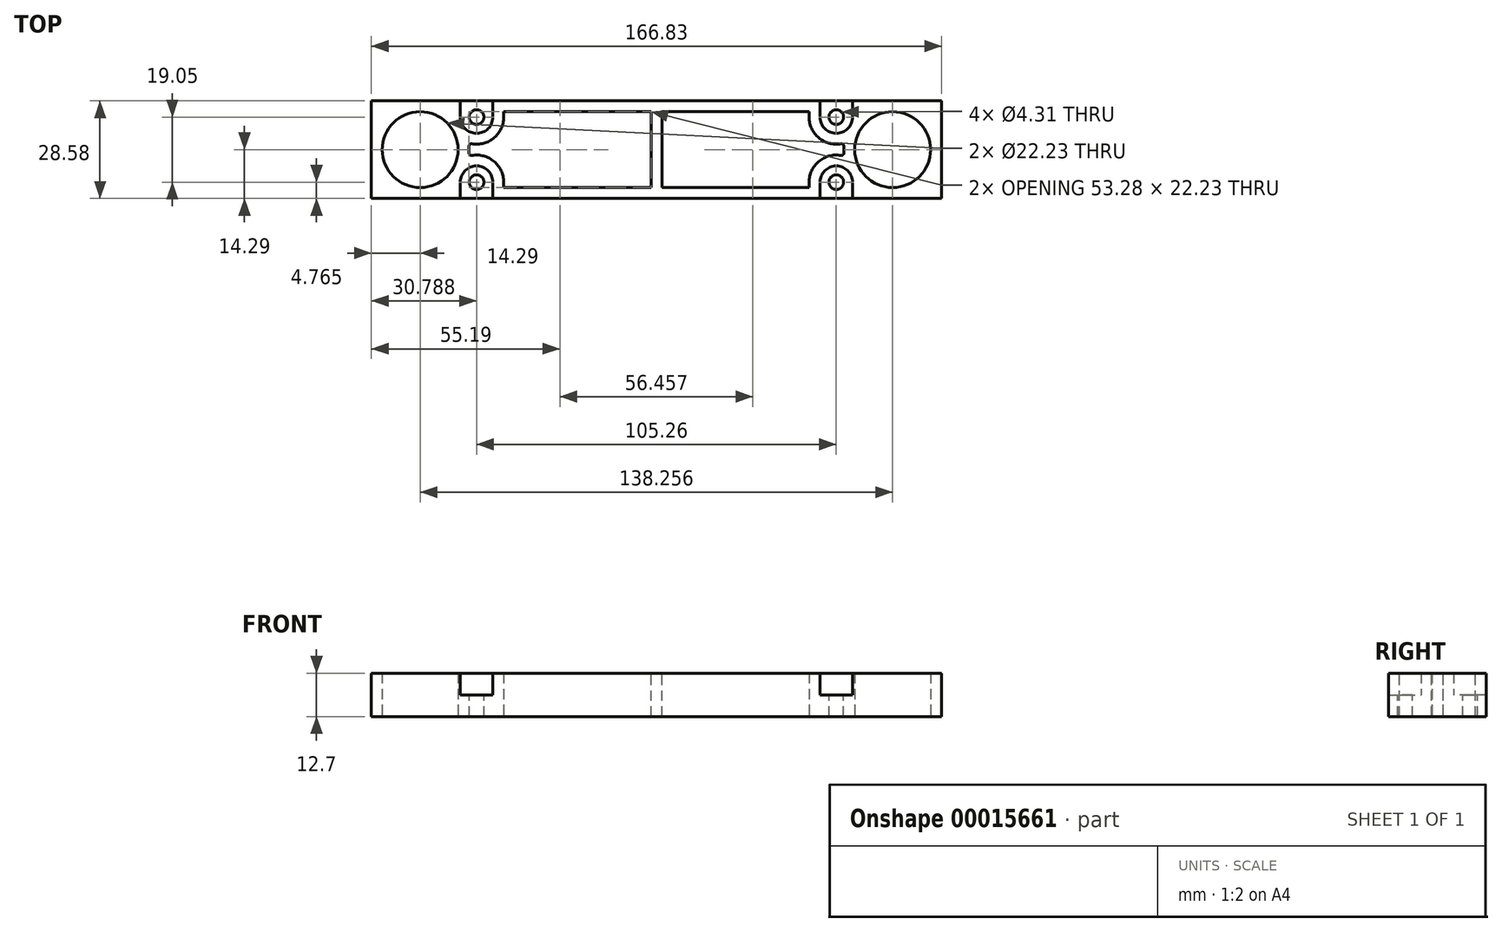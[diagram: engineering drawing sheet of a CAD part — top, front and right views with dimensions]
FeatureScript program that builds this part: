
annotation { "Feature Type Name" : "Feature", "Feature Type Description" : "" }
export const myFeature = defineFeature(function(context is Context, id is Id, definition is map)
    precondition{}
    {
        {
            var Q0;
            Q0=qCreatedBy(makeId("Top.planeOp"),FACE);
            var sketch = newSketch(context, id + "F0", { "sketchPlane" : qUnion([Q0])});
            skCircle(sketch, "E0", {"center": v(0, 0) * mm, "radius": 11.11 * mm});
            skLineSegment(sketch, "E1", {"start": v(0, 0) * mm, "end": v(138.26, 0) * mm, "construction": true});
            skLineSegment(sketch, "E2.left", {"start": v(-14.29, 14.29) * mm, "end": v(-14.29, -14.29) * mm});
            skLineSegment(sketch, "E2.right", {"start": v(152.54, 14.29) * mm, "end": v(152.54, -14.29) * mm});
            skPoint(sketch, "E2.middle", {"position": v(69.13, 0) * mm});
            skLineSegment(sketch, "E3", {"start": v(138.26, 0) * mm, "end": v(152.54, 0) * mm, "construction": true});
            skLineSegment(sketch, "E4", {"start": v(0, 0) * mm, "end": v(-14.29, 0) * mm, "construction": true});
            skCircle(sketch, "E5", {"center": v(138.26, 0) * mm, "radius": 11.11 * mm});
            skLineSegment(sketch, "E6", {"start": v(-14.29, 14.29) * mm, "end": v(11.74, 14.29) * mm});
            skLineSegment(sketch, "E7", {"start": v(152.54, 14.29) * mm, "end": v(126.52, 14.29) * mm});
            skLineSegment(sketch, "E8.bottom", {"start": v(11.74, 14.29) * mm, "end": v(21.26, 14.29) * mm, "construction": true});
            skLineSegment(sketch, "E8.top", {"start": v(11.74, 9.53) * mm, "end": v(21.26, 9.53) * mm, "construction": true});
            skLineSegment(sketch, "E8.left", {"start": v(11.74, 14.29) * mm, "end": v(11.74, 9.52) * mm});
            skLineSegment(sketch, "E8.right", {"start": v(21.26, 14.29) * mm, "end": v(21.26, 9.52) * mm});
            skLineSegment(sketch, "E9.bottom", {"start": v(126.52, 14.29) * mm, "end": v(117, 14.29) * mm, "construction": true});
            skLineSegment(sketch, "E9.top", {"start": v(126.52, 9.52) * mm, "end": v(117, 9.52) * mm, "construction": true});
            skLineSegment(sketch, "E9.left", {"start": v(126.52, 14.29) * mm, "end": v(126.52, 9.53) * mm});
            skLineSegment(sketch, "E9.right", {"start": v(117, 14.29) * mm, "end": v(117, 9.53) * mm});
            skCircle(sketch, "E10", {"center": v(16.5, 9.53) * mm, "radius": 7.94 * mm, "construction": true});
            skArc(sketch, "E11", {"start": v(21.26, 9.52) * mm, "mid": v(16.5, 14.29) * mm, "end": v(11.74, 9.53) * mm, "construction": true});
            skArc(sketch, "E12", {"start": v(11.74, 9.52) * mm, "mid": v(16.5, 4.76) * mm, "end": v(21.26, 9.52) * mm});
            skArc(sketch, "E13", {"start": v(117, 9.53) * mm, "mid": v(121.76, 4.76) * mm, "end": v(126.52, 9.53) * mm});
            skLineSegment(sketch, "E14", {"start": v(21.26, 14.29) * mm, "end": v(117, 14.29) * mm});
            skLineSegment(sketch, "E15", {"start": v(-14.29, -14.29) * mm, "end": v(11.74, -14.29) * mm});
            skLineSegment(sketch, "E16", {"start": v(152.54, -14.29) * mm, "end": v(126.52, -14.29) * mm});
            skLineSegment(sketch, "E17.bottom", {"start": v(11.74, -14.29) * mm, "end": v(21.26, -14.29) * mm, "construction": true});
            skLineSegment(sketch, "E17.top", {"start": v(11.74, -9.52) * mm, "end": v(21.26, -9.52) * mm, "construction": true});
            skLineSegment(sketch, "E17.left", {"start": v(11.74, -14.29) * mm, "end": v(11.74, -9.52) * mm});
            skLineSegment(sketch, "E17.right", {"start": v(21.26, -14.29) * mm, "end": v(21.26, -9.53) * mm});
            skLineSegment(sketch, "E18.bottom", {"start": v(126.52, -14.29) * mm, "end": v(117, -14.29) * mm, "construction": true});
            skLineSegment(sketch, "E18.top", {"start": v(126.52, -9.52) * mm, "end": v(117, -9.52) * mm, "construction": true});
            skLineSegment(sketch, "E18.left", {"start": v(126.52, -14.29) * mm, "end": v(126.52, -9.53) * mm});
            skLineSegment(sketch, "E18.right", {"start": v(117, -14.29) * mm, "end": v(117, -9.53) * mm});
            skLineSegment(sketch, "E19", {"start": v(21.26, -14.29) * mm, "end": v(117, -14.29) * mm});
            skArc(sketch, "E20", {"start": v(21.26, -9.53) * mm, "mid": v(16.5, -4.76) * mm, "end": v(11.74, -9.52) * mm});
            skArc(sketch, "E21", {"start": v(126.52, -9.53) * mm, "mid": v(121.76, -4.76) * mm, "end": v(117, -9.53) * mm});
            skSolve(sketch);
        }
        {
            var Q0;
            Q0 = qSketchRegion(id + "F0", true);
            extrude(context, id + "F1", {"entities" : qUnion([Q0]), "depth" : 6.35 * mm});
        }
        {
            var Q0;
            Q0=makeQuery(id+"F1.opExtrude","CAP_FACE",FACE,{"disambiguationData":[OSD([sQuery(id+"F0.wireOp",EDGE,"E0"),sQuery(id+"F0.wireOp",EDGE,"E2.left"),sQuery(id+"F0.wireOp",EDGE,"E2.right"),sQuery(id+"F0.wireOp",EDGE,"E5"),sQuery(id+"F0.wireOp",EDGE,"E6"),sQuery(id+"F0.wireOp",EDGE,"E7"),sQuery(id+"F0.wireOp",EDGE,"E8.left"),sQuery(id+"F0.wireOp",EDGE,"E8.right"),sQuery(id+"F0.wireOp",EDGE,"E9.left"),sQuery(id+"F0.wireOp",EDGE,"E9.right"),sQuery(id+"F0.wireOp",EDGE,"E12"),sQuery(id+"F0.wireOp",EDGE,"E13"),sQuery(id+"F0.wireOp",EDGE,"E14"),sQuery(id+"F0.wireOp",EDGE,"E15"),sQuery(id+"F0.wireOp",EDGE,"E16"),sQuery(id+"F0.wireOp",EDGE,"E17.left"),sQuery(id+"F0.wireOp",EDGE,"E17.right"),sQuery(id+"F0.wireOp",EDGE,"E18.left"),sQuery(id+"F0.wireOp",EDGE,"E18.right"),sQuery(id+"F0.wireOp",EDGE,"E19"),sQuery(id+"F0.wireOp",EDGE,"E20"),sQuery(id+"F0.wireOp",EDGE,"E21")])],"isStart":false});
            shell(context, id + "F2", {"entities" : qUnion([Q0]), "thickness" : 3.17 * mm});
        }
        {
            var Q0;
            Q0=makeQuery(id+"F2.opShell","OFFSET_FACE",FACE,{"disambiguationData":[OSD([sQuery(id+"F0.wireOp",EDGE,"E0"),sQuery(id+"F0.wireOp",EDGE,"E2.left"),sQuery(id+"F0.wireOp",EDGE,"E2.right"),sQuery(id+"F0.wireOp",EDGE,"E5"),sQuery(id+"F0.wireOp",EDGE,"E6"),sQuery(id+"F0.wireOp",EDGE,"E7"),sQuery(id+"F0.wireOp",EDGE,"E8.left"),sQuery(id+"F0.wireOp",EDGE,"E8.right"),sQuery(id+"F0.wireOp",EDGE,"E9.left"),sQuery(id+"F0.wireOp",EDGE,"E9.right"),sQuery(id+"F0.wireOp",EDGE,"E12"),sQuery(id+"F0.wireOp",EDGE,"E13"),sQuery(id+"F0.wireOp",EDGE,"E14"),sQuery(id+"F0.wireOp",EDGE,"E15"),sQuery(id+"F0.wireOp",EDGE,"E16"),sQuery(id+"F0.wireOp",EDGE,"E17.left"),sQuery(id+"F0.wireOp",EDGE,"E17.right"),sQuery(id+"F0.wireOp",EDGE,"E18.left"),sQuery(id+"F0.wireOp",EDGE,"E18.right"),sQuery(id+"F0.wireOp",EDGE,"E19"),sQuery(id+"F0.wireOp",EDGE,"E20"),sQuery(id+"F0.wireOp",EDGE,"E21")]),OD(0.0)]});
            var Q1;
            Q1=makeQuery(id+"F2.opShell","OFFSET_FACE",FACE,{"disambiguationData":[OSD([sQuery(id+"F0.wireOp",EDGE,"E0"),sQuery(id+"F0.wireOp",EDGE,"E2.left"),sQuery(id+"F0.wireOp",EDGE,"E2.right"),sQuery(id+"F0.wireOp",EDGE,"E5"),sQuery(id+"F0.wireOp",EDGE,"E6"),sQuery(id+"F0.wireOp",EDGE,"E7"),sQuery(id+"F0.wireOp",EDGE,"E8.left"),sQuery(id+"F0.wireOp",EDGE,"E8.right"),sQuery(id+"F0.wireOp",EDGE,"E9.left"),sQuery(id+"F0.wireOp",EDGE,"E9.right"),sQuery(id+"F0.wireOp",EDGE,"E12"),sQuery(id+"F0.wireOp",EDGE,"E13"),sQuery(id+"F0.wireOp",EDGE,"E14"),sQuery(id+"F0.wireOp",EDGE,"E15"),sQuery(id+"F0.wireOp",EDGE,"E16"),sQuery(id+"F0.wireOp",EDGE,"E17.left"),sQuery(id+"F0.wireOp",EDGE,"E17.right"),sQuery(id+"F0.wireOp",EDGE,"E18.left"),sQuery(id+"F0.wireOp",EDGE,"E18.right"),sQuery(id+"F0.wireOp",EDGE,"E19"),sQuery(id+"F0.wireOp",EDGE,"E20"),sQuery(id+"F0.wireOp",EDGE,"E21")]),OD(3.0)]});
            var Q2;
            Q2=makeQuery(id+"F2.opShell","OFFSET_FACE",FACE,{"disambiguationData":[OSD([sQuery(id+"F0.wireOp",EDGE,"E0"),sQuery(id+"F0.wireOp",EDGE,"E2.left"),sQuery(id+"F0.wireOp",EDGE,"E2.right"),sQuery(id+"F0.wireOp",EDGE,"E5"),sQuery(id+"F0.wireOp",EDGE,"E6"),sQuery(id+"F0.wireOp",EDGE,"E7"),sQuery(id+"F0.wireOp",EDGE,"E8.left"),sQuery(id+"F0.wireOp",EDGE,"E8.right"),sQuery(id+"F0.wireOp",EDGE,"E9.left"),sQuery(id+"F0.wireOp",EDGE,"E9.right"),sQuery(id+"F0.wireOp",EDGE,"E12"),sQuery(id+"F0.wireOp",EDGE,"E13"),sQuery(id+"F0.wireOp",EDGE,"E14"),sQuery(id+"F0.wireOp",EDGE,"E15"),sQuery(id+"F0.wireOp",EDGE,"E16"),sQuery(id+"F0.wireOp",EDGE,"E17.left"),sQuery(id+"F0.wireOp",EDGE,"E17.right"),sQuery(id+"F0.wireOp",EDGE,"E18.left"),sQuery(id+"F0.wireOp",EDGE,"E18.right"),sQuery(id+"F0.wireOp",EDGE,"E19"),sQuery(id+"F0.wireOp",EDGE,"E20"),sQuery(id+"F0.wireOp",EDGE,"E21")]),OD(4.0)]});
            var Q3;
            Q3=makeQuery(id+"F2.opShell","OFFSET_FACE",FACE,{"disambiguationData":[OSD([sQuery(id+"F0.wireOp",EDGE,"E0"),sQuery(id+"F0.wireOp",EDGE,"E2.left"),sQuery(id+"F0.wireOp",EDGE,"E2.right"),sQuery(id+"F0.wireOp",EDGE,"E5"),sQuery(id+"F0.wireOp",EDGE,"E6"),sQuery(id+"F0.wireOp",EDGE,"E7"),sQuery(id+"F0.wireOp",EDGE,"E8.left"),sQuery(id+"F0.wireOp",EDGE,"E8.right"),sQuery(id+"F0.wireOp",EDGE,"E9.left"),sQuery(id+"F0.wireOp",EDGE,"E9.right"),sQuery(id+"F0.wireOp",EDGE,"E12"),sQuery(id+"F0.wireOp",EDGE,"E13"),sQuery(id+"F0.wireOp",EDGE,"E14"),sQuery(id+"F0.wireOp",EDGE,"E15"),sQuery(id+"F0.wireOp",EDGE,"E16"),sQuery(id+"F0.wireOp",EDGE,"E17.left"),sQuery(id+"F0.wireOp",EDGE,"E17.right"),sQuery(id+"F0.wireOp",EDGE,"E18.left"),sQuery(id+"F0.wireOp",EDGE,"E18.right"),sQuery(id+"F0.wireOp",EDGE,"E19"),sQuery(id+"F0.wireOp",EDGE,"E20"),sQuery(id+"F0.wireOp",EDGE,"E21")]),OD(1.0)]});
            var Q4;
            Q4=makeQuery(id+"F1.opExtrude","CAP_FACE",FACE,{"disambiguationData":[OSD([sQuery(id+"F0.wireOp",EDGE,"E0"),sQuery(id+"F0.wireOp",EDGE,"E2.left"),sQuery(id+"F0.wireOp",EDGE,"E2.right"),sQuery(id+"F0.wireOp",EDGE,"E5"),sQuery(id+"F0.wireOp",EDGE,"E6"),sQuery(id+"F0.wireOp",EDGE,"E7"),sQuery(id+"F0.wireOp",EDGE,"E8.left"),sQuery(id+"F0.wireOp",EDGE,"E8.right"),sQuery(id+"F0.wireOp",EDGE,"E9.left"),sQuery(id+"F0.wireOp",EDGE,"E9.right"),sQuery(id+"F0.wireOp",EDGE,"E12"),sQuery(id+"F0.wireOp",EDGE,"E13"),sQuery(id+"F0.wireOp",EDGE,"E14"),sQuery(id+"F0.wireOp",EDGE,"E15"),sQuery(id+"F0.wireOp",EDGE,"E16"),sQuery(id+"F0.wireOp",EDGE,"E17.left"),sQuery(id+"F0.wireOp",EDGE,"E17.right"),sQuery(id+"F0.wireOp",EDGE,"E18.left"),sQuery(id+"F0.wireOp",EDGE,"E18.right"),sQuery(id+"F0.wireOp",EDGE,"E19"),sQuery(id+"F0.wireOp",EDGE,"E20"),sQuery(id+"F0.wireOp",EDGE,"E21")])],"isStart":false});
            extrude(context, id + "F3", {"entities" : qUnion([Q0, Q1, Q2, Q3]), "operationType" : NewBodyOperationType.ADD, "endBound" : BoundingType.UP_TO_SURFACE, "endBoundEntityFace" : qUnion([Q4]), "depth" : 25.4 * mm});
        }
        {
            var Q0;
            Q0=makeQuery(id+"F2.opShell","OFFSET_FACE",FACE,{"disambiguationData":[OSD([sQuery(id+"F0.wireOp",EDGE,"E0"),sQuery(id+"F0.wireOp",EDGE,"E2.left"),sQuery(id+"F0.wireOp",EDGE,"E2.right"),sQuery(id+"F0.wireOp",EDGE,"E5"),sQuery(id+"F0.wireOp",EDGE,"E6"),sQuery(id+"F0.wireOp",EDGE,"E7"),sQuery(id+"F0.wireOp",EDGE,"E8.left"),sQuery(id+"F0.wireOp",EDGE,"E8.right"),sQuery(id+"F0.wireOp",EDGE,"E9.left"),sQuery(id+"F0.wireOp",EDGE,"E9.right"),sQuery(id+"F0.wireOp",EDGE,"E12"),sQuery(id+"F0.wireOp",EDGE,"E13"),sQuery(id+"F0.wireOp",EDGE,"E14"),sQuery(id+"F0.wireOp",EDGE,"E15"),sQuery(id+"F0.wireOp",EDGE,"E16"),sQuery(id+"F0.wireOp",EDGE,"E17.left"),sQuery(id+"F0.wireOp",EDGE,"E17.right"),sQuery(id+"F0.wireOp",EDGE,"E18.left"),sQuery(id+"F0.wireOp",EDGE,"E18.right"),sQuery(id+"F0.wireOp",EDGE,"E19"),sQuery(id+"F0.wireOp",EDGE,"E20"),sQuery(id+"F0.wireOp",EDGE,"E21")]),OD(2.0)]});
            var Q1;
            Q1=makeQuery(id+"F1.opExtrude","CAP_FACE",FACE,{"disambiguationData":[OSD([sQuery(id+"F0.wireOp",EDGE,"E0"),sQuery(id+"F0.wireOp",EDGE,"E2.left"),sQuery(id+"F0.wireOp",EDGE,"E2.right"),sQuery(id+"F0.wireOp",EDGE,"E5"),sQuery(id+"F0.wireOp",EDGE,"E6"),sQuery(id+"F0.wireOp",EDGE,"E7"),sQuery(id+"F0.wireOp",EDGE,"E8.left"),sQuery(id+"F0.wireOp",EDGE,"E8.right"),sQuery(id+"F0.wireOp",EDGE,"E9.left"),sQuery(id+"F0.wireOp",EDGE,"E9.right"),sQuery(id+"F0.wireOp",EDGE,"E12"),sQuery(id+"F0.wireOp",EDGE,"E13"),sQuery(id+"F0.wireOp",EDGE,"E14"),sQuery(id+"F0.wireOp",EDGE,"E15"),sQuery(id+"F0.wireOp",EDGE,"E16"),sQuery(id+"F0.wireOp",EDGE,"E17.left"),sQuery(id+"F0.wireOp",EDGE,"E17.right"),sQuery(id+"F0.wireOp",EDGE,"E18.left"),sQuery(id+"F0.wireOp",EDGE,"E18.right"),sQuery(id+"F0.wireOp",EDGE,"E19"),sQuery(id+"F0.wireOp",EDGE,"E20"),sQuery(id+"F0.wireOp",EDGE,"E21")])],"isStart":true});
            extrude(context, id + "F4", {"entities" : qUnion([Q0]), "operationType" : NewBodyOperationType.REMOVE, "endBound" : BoundingType.UP_TO_SURFACE, "oppositeDirection" : true, "endBoundEntityFace" : qUnion([Q1]), "depth" : 25.4 * mm});
        }
        {
            var Q0;
            Q0=makeQuery(id+"F1.opExtrude","CAP_FACE",FACE,{"disambiguationData":[OSD([sQuery(id+"F0.wireOp",EDGE,"E0"),sQuery(id+"F0.wireOp",EDGE,"E2.left"),sQuery(id+"F0.wireOp",EDGE,"E2.right"),sQuery(id+"F0.wireOp",EDGE,"E5"),sQuery(id+"F0.wireOp",EDGE,"E6"),sQuery(id+"F0.wireOp",EDGE,"E7"),sQuery(id+"F0.wireOp",EDGE,"E8.left"),sQuery(id+"F0.wireOp",EDGE,"E8.right"),sQuery(id+"F0.wireOp",EDGE,"E9.left"),sQuery(id+"F0.wireOp",EDGE,"E9.right"),sQuery(id+"F0.wireOp",EDGE,"E12"),sQuery(id+"F0.wireOp",EDGE,"E13"),sQuery(id+"F0.wireOp",EDGE,"E14"),sQuery(id+"F0.wireOp",EDGE,"E15"),sQuery(id+"F0.wireOp",EDGE,"E16"),sQuery(id+"F0.wireOp",EDGE,"E17.left"),sQuery(id+"F0.wireOp",EDGE,"E17.right"),sQuery(id+"F0.wireOp",EDGE,"E18.left"),sQuery(id+"F0.wireOp",EDGE,"E18.right"),sQuery(id+"F0.wireOp",EDGE,"E19"),sQuery(id+"F0.wireOp",EDGE,"E20"),sQuery(id+"F0.wireOp",EDGE,"E21")])],"isStart":true});
            var sketch = newSketch(context, id + "F5", { "sketchPlane" : qUnion([Q0])});
            skLineSegment(sketch, "E22.bottom", {"start": v(11.74, -14.29) * mm, "end": v(126.52, -14.29) * mm});
            skLineSegment(sketch, "E22.top", {"start": v(11.74, 14.29) * mm, "end": v(126.52, 14.29) * mm});
            skLineSegment(sketch, "E22.left", {"start": v(11.74, -14.29) * mm, "end": v(11.74, 14.29) * mm, "construction": true});
            skLineSegment(sketch, "E22.right", {"start": v(126.52, -14.29) * mm, "end": v(126.52, 14.29) * mm, "construction": true});
            skCircle(sketch, "E23", {"center": v(16.5, 9.52) * mm, "radius": 2.15 * mm});
            skCircle(sketch, "E24", {"center": v(16.5, -9.53) * mm, "radius": 2.15 * mm});
            skCircle(sketch, "E25", {"center": v(121.76, 9.53) * mm, "radius": 2.15 * mm});
            skCircle(sketch, "E26", {"center": v(121.76, -9.53) * mm, "radius": 2.15 * mm});
            skSolve(sketch);
        }
        {
            var Q0;
            {var subQ19=sQuery(id+"F0.wireOp",EDGE,"E0");var subQ20=makeQuery(id+"F1.opExtrude","CAP_EDGE",EDGE,{"disambiguationData":[OSD([subQ19])],"isStart":true});Q0=makeQuery(id+"F5.imprint","IMPRINT",FACE,{"disambiguationData":[TD([[makeQuery(id+"F5.imprint","IMPRINT",EDGE,{"derivedFrom":subQ20}),1.0]])]});}
            var Q1;
            Q1=makeQuery(id+"F5.imprint","IMPRINT",FACE,{"disambiguationData":[TD([[makeQuery(id+"F5.imprint","IMPRINT",EDGE,{"derivedFrom":sQuery(id+"F5.wireOp",EDGE,"E24")}),-1.0]])]});
            var Q2;
            Q2=makeQuery(id+"F5.imprint","IMPRINT",FACE,{"disambiguationData":[TD([[makeQuery(id+"F5.imprint","IMPRINT",EDGE,{"derivedFrom":sQuery(id+"F5.wireOp",EDGE,"E26")}),-1.0]])]});
            var Q3;
            Q3=makeQuery(id+"F5.imprint","IMPRINT",FACE,{"disambiguationData":[TD([[makeQuery(id+"F5.imprint","IMPRINT",EDGE,{"derivedFrom":sQuery(id+"F5.wireOp",EDGE,"E25")}),-1.0]])]});
            var Q4;
            Q4=makeQuery(id+"F5.imprint","IMPRINT",FACE,{"disambiguationData":[TD([[makeQuery(id+"F5.imprint","IMPRINT",EDGE,{"derivedFrom":sQuery(id+"F5.wireOp",EDGE,"E23")}),-1.0]])]});
            extrude(context, id + "F6", {"entities" : qUnion([Q0, Q1, Q2, Q3, Q4]), "operationType" : NewBodyOperationType.ADD, "depth" : 6.35 * mm});
        }
        {
            var Q0;
            {var subQ0=sQuery(id+"F0.wireOp",EDGE,"E21");var subQ1=sQuery(id+"F0.wireOp",EDGE,"E20");var subQ2=sQuery(id+"F0.wireOp",EDGE,"E19");var subQ3=sQuery(id+"F0.wireOp",EDGE,"E18.right");var subQ4=sQuery(id+"F0.wireOp",EDGE,"E18.left");var subQ5=sQuery(id+"F0.wireOp",EDGE,"E17.right");var subQ6=sQuery(id+"F0.wireOp",EDGE,"E17.left");var subQ7=sQuery(id+"F0.wireOp",EDGE,"E16");var subQ8=sQuery(id+"F0.wireOp",EDGE,"E15");var subQ9=sQuery(id+"F0.wireOp",EDGE,"E14");var subQ10=sQuery(id+"F0.wireOp",EDGE,"E13");var subQ11=sQuery(id+"F0.wireOp",EDGE,"E12");var subQ12=sQuery(id+"F0.wireOp",EDGE,"E9.right");var subQ13=sQuery(id+"F0.wireOp",EDGE,"E9.left");var subQ14=sQuery(id+"F0.wireOp",EDGE,"E8.right");var subQ15=sQuery(id+"F0.wireOp",EDGE,"E8.left");var subQ16=sQuery(id+"F0.wireOp",EDGE,"E7");var subQ17=sQuery(id+"F0.wireOp",EDGE,"E6");var subQ18=sQuery(id+"F0.wireOp",EDGE,"E5");var subQ19=sQuery(id+"F0.wireOp",EDGE,"E2.right");var subQ20=sQuery(id+"F0.wireOp",EDGE,"E2.left");var subQ21=sQuery(id+"F0.wireOp",EDGE,"E0");Q0=makeQuery(id+"F3.boolean.opBoolean","MERGE",FACE,{"derivedFrom":[makeQuery(id+"F1.opExtrude","CAP_FACE",FACE,{"disambiguationData":[OSD([subQ21,subQ20,subQ19,subQ18,subQ17,subQ16,subQ15,subQ14,subQ13,subQ12,subQ11,subQ10,subQ9,subQ8,subQ7,subQ6,subQ5,subQ4,subQ3,subQ2,subQ1,subQ0])],"isStart":false}),makeQuery(id+"F3.opExtrude","CAP_FACE",FACE,{"disambiguationData":[OSD([subQ21,subQ20,subQ19,subQ18,subQ17,subQ16,subQ15,subQ14,subQ13,subQ12,subQ11,subQ10,subQ9,subQ8,subQ7,subQ6,subQ5,subQ4,subQ3,subQ2,subQ1,subQ0]),ownerDisambiguation([makeQuery(id+"F3.opExtrude","SWEPT_BODY",BODY,{"disambiguationData":[OSD([subQ21,subQ20,subQ19,subQ18,subQ17,subQ16,subQ15,subQ14,subQ13,subQ12,subQ11,subQ10,subQ9,subQ8,subQ7,subQ6,subQ5,subQ4,subQ3,subQ2,subQ1,subQ0]),TDD([makeQuery(id+"F2.opShell","OFFSET_FACE",FACE,{"disambiguationData":[OSD([subQ21,subQ20,subQ19,subQ18,subQ17,subQ16,subQ15,subQ14,subQ13,subQ12,subQ11,subQ10,subQ9,subQ8,subQ7,subQ6,subQ5,subQ4,subQ3,subQ2,subQ1,subQ0]),OD(0.0)]})])]})])],"isStart":false}),makeQuery(id+"F3.opExtrude","CAP_FACE",FACE,{"disambiguationData":[OSD([subQ21,subQ20,subQ19,subQ18,subQ17,subQ16,subQ15,subQ14,subQ13,subQ12,subQ11,subQ10,subQ9,subQ8,subQ7,subQ6,subQ5,subQ4,subQ3,subQ2,subQ1,subQ0]),ownerDisambiguation([makeQuery(id+"F3.opExtrude","SWEPT_BODY",BODY,{"disambiguationData":[OSD([subQ21,subQ20,subQ19,subQ18,subQ17,subQ16,subQ15,subQ14,subQ13,subQ12,subQ11,subQ10,subQ9,subQ8,subQ7,subQ6,subQ5,subQ4,subQ3,subQ2,subQ1,subQ0]),TDD([makeQuery(id+"F2.opShell","OFFSET_FACE",FACE,{"disambiguationData":[OSD([subQ21,subQ20,subQ19,subQ18,subQ17,subQ16,subQ15,subQ14,subQ13,subQ12,subQ11,subQ10,subQ9,subQ8,subQ7,subQ6,subQ5,subQ4,subQ3,subQ2,subQ1,subQ0]),OD(1.0)]})])]})])],"isStart":false}),makeQuery(id+"F3.opExtrude","CAP_FACE",FACE,{"disambiguationData":[OSD([subQ21,subQ20,subQ19,subQ18,subQ17,subQ16,subQ15,subQ14,subQ13,subQ12,subQ11,subQ10,subQ9,subQ8,subQ7,subQ6,subQ5,subQ4,subQ3,subQ2,subQ1,subQ0]),ownerDisambiguation([makeQuery(id+"F3.opExtrude","SWEPT_BODY",BODY,{"disambiguationData":[OSD([subQ21,subQ20,subQ19,subQ18,subQ17,subQ16,subQ15,subQ14,subQ13,subQ12,subQ11,subQ10,subQ9,subQ8,subQ7,subQ6,subQ5,subQ4,subQ3,subQ2,subQ1,subQ0]),TDD([makeQuery(id+"F2.opShell","OFFSET_FACE",FACE,{"disambiguationData":[OSD([subQ21,subQ20,subQ19,subQ18,subQ17,subQ16,subQ15,subQ14,subQ13,subQ12,subQ11,subQ10,subQ9,subQ8,subQ7,subQ6,subQ5,subQ4,subQ3,subQ2,subQ1,subQ0]),OD(3.0)]})])]})])],"isStart":false}),makeQuery(id+"F3.opExtrude","CAP_FACE",FACE,{"disambiguationData":[OSD([subQ21,subQ20,subQ19,subQ18,subQ17,subQ16,subQ15,subQ14,subQ13,subQ12,subQ11,subQ10,subQ9,subQ8,subQ7,subQ6,subQ5,subQ4,subQ3,subQ2,subQ1,subQ0]),ownerDisambiguation([makeQuery(id+"F3.opExtrude","SWEPT_BODY",BODY,{"disambiguationData":[OSD([subQ21,subQ20,subQ19,subQ18,subQ17,subQ16,subQ15,subQ14,subQ13,subQ12,subQ11,subQ10,subQ9,subQ8,subQ7,subQ6,subQ5,subQ4,subQ3,subQ2,subQ1,subQ0]),TDD([makeQuery(id+"F2.opShell","OFFSET_FACE",FACE,{"disambiguationData":[OSD([subQ21,subQ20,subQ19,subQ18,subQ17,subQ16,subQ15,subQ14,subQ13,subQ12,subQ11,subQ10,subQ9,subQ8,subQ7,subQ6,subQ5,subQ4,subQ3,subQ2,subQ1,subQ0]),OD(4.0)]})])]})])],"isStart":false})]});}
            var sketch = newSketch(context, id + "F7", { "sketchPlane" : qUnion([Q0])});
            skLineSegment(sketch, "E27.bottom", {"start": v(67.54, 11.11) * mm, "end": v(70.72, 11.11) * mm});
            skLineSegment(sketch, "E27.top", {"start": v(67.54, -11.11) * mm, "end": v(70.72, -11.11) * mm});
            skLineSegment(sketch, "E27.left", {"start": v(67.54, 11.11) * mm, "end": v(67.54, -11.11) * mm});
            skLineSegment(sketch, "E27.right", {"start": v(70.72, 11.11) * mm, "end": v(70.72, -11.11) * mm});
            skPoint(sketch, "E28", {"position": v(69.13, 11.11) * mm});
            skSolve(sketch);
        }
        {
            var Q0;
            Q0 = qSketchRegion(id + "F7", true);
            var Q1;
            Q1=makeQuery(id+"F6.opExtrude","CAP_FACE",FACE,{"disambiguationData":[OSD([sQuery(id+"F0.wireOp",EDGE,"E0"),sQuery(id+"F0.wireOp",EDGE,"E2.left"),sQuery(id+"F0.wireOp",EDGE,"E2.right"),sQuery(id+"F0.wireOp",EDGE,"E5"),sQuery(id+"F0.wireOp",EDGE,"E6"),sQuery(id+"F0.wireOp",EDGE,"E7"),sQuery(id+"F0.wireOp",EDGE,"E8.left"),sQuery(id+"F0.wireOp",EDGE,"E8.right"),sQuery(id+"F0.wireOp",EDGE,"E9.left"),sQuery(id+"F0.wireOp",EDGE,"E9.right"),sQuery(id+"F0.wireOp",EDGE,"E12"),sQuery(id+"F0.wireOp",EDGE,"E13"),sQuery(id+"F0.wireOp",EDGE,"E14"),sQuery(id+"F0.wireOp",EDGE,"E15"),sQuery(id+"F0.wireOp",EDGE,"E16"),sQuery(id+"F0.wireOp",EDGE,"E17.left"),sQuery(id+"F0.wireOp",EDGE,"E17.right"),sQuery(id+"F0.wireOp",EDGE,"E18.left"),sQuery(id+"F0.wireOp",EDGE,"E18.right"),sQuery(id+"F0.wireOp",EDGE,"E19"),sQuery(id+"F0.wireOp",EDGE,"E20"),sQuery(id+"F0.wireOp",EDGE,"E21"),sQuery(id+"F5.wireOp",EDGE,"E22.bottom"),sQuery(id+"F5.wireOp",EDGE,"E22.top"),sQuery(id+"F5.wireOp",EDGE,"E23"),sQuery(id+"F5.wireOp",EDGE,"E24"),sQuery(id+"F5.wireOp",EDGE,"E25"),sQuery(id+"F5.wireOp",EDGE,"E26")])],"isStart":false});
            extrude(context, id + "F8", {"entities" : qUnion([Q0]), "operationType" : NewBodyOperationType.ADD, "endBound" : BoundingType.UP_TO_SURFACE, "oppositeDirection" : true, "endBoundEntityFace" : qUnion([Q1]), "depth" : 25.4 * mm});
        }
        {
            var Q0;
            {var subQ0=sQuery(id+"F0.wireOp",EDGE,"E0");var subQ1=sQuery(id+"F0.wireOp",EDGE,"E21");var subQ2=sQuery(id+"F0.wireOp",EDGE,"E20");var subQ3=sQuery(id+"F0.wireOp",EDGE,"E19");var subQ4=sQuery(id+"F0.wireOp",EDGE,"E18.right");var subQ5=sQuery(id+"F0.wireOp",EDGE,"E18.left");var subQ6=sQuery(id+"F0.wireOp",EDGE,"E17.right");var subQ7=sQuery(id+"F0.wireOp",EDGE,"E17.left");var subQ8=sQuery(id+"F0.wireOp",EDGE,"E16");var subQ9=sQuery(id+"F0.wireOp",EDGE,"E15");var subQ10=sQuery(id+"F0.wireOp",EDGE,"E14");var subQ11=sQuery(id+"F0.wireOp",EDGE,"E13");var subQ12=sQuery(id+"F0.wireOp",EDGE,"E12");var subQ13=sQuery(id+"F0.wireOp",EDGE,"E9.right");var subQ14=sQuery(id+"F0.wireOp",EDGE,"E9.left");var subQ15=sQuery(id+"F0.wireOp",EDGE,"E8.right");var subQ16=sQuery(id+"F0.wireOp",EDGE,"E8.left");var subQ17=sQuery(id+"F0.wireOp",EDGE,"E7");var subQ18=sQuery(id+"F0.wireOp",EDGE,"E6");var subQ19=sQuery(id+"F0.wireOp",EDGE,"E5");var subQ20=sQuery(id+"F0.wireOp",EDGE,"E2.right");var subQ21=sQuery(id+"F0.wireOp",EDGE,"E2.left");var subQ22=makeQuery(id+"F1.opExtrude","CAP_FACE",FACE,{"disambiguationData":[OSD([subQ0,subQ21,subQ20,subQ19,subQ18,subQ17,subQ16,subQ15,subQ14,subQ13,subQ12,subQ11,subQ10,subQ9,subQ8,subQ7,subQ6,subQ5,subQ4,subQ3,subQ2,subQ1])],"isStart":true});var subQ23=makeQuery(id+"F1.opExtrude","SWEPT_FACE",FACE,{"disambiguationData":[OSD([subQ12])]});var subQ24=makeQuery(id+"F1.opExtrude","SWEPT_FACE",FACE,{"disambiguationData":[OSD([subQ0])]});Q0=makeQuery(id+"F6.boolean.opBoolean","MERGE",EDGE,{"derivedFrom":[makeQuery(id+"F4.boolean.opBoolean","MERGE",EDGE,{"derivedFrom":[makeQuery(id+"F2.opShell","TWEAK_EDGE",EDGE,{"derivedFrom":[subQ24,subQ23]}),makeQuery(id+"F4.opExtrude","SWEPT_EDGE",EDGE,{"disambiguationData":[OSD([subQ0,subQ21,subQ20,subQ19,subQ18,subQ17,subQ16,subQ15,subQ14,subQ13,subQ12,subQ11,subQ10,subQ9,subQ8,subQ7,subQ6,subQ5,subQ4,subQ3,subQ2,subQ1]),TDD([makeQuery(id+"F2.opShell","TWEAK_VERTEX",VERTEX,{"derivedFrom":[subQ24,subQ22,subQ23]})])]})]}),makeQuery(id+"F6.opExtrude","SWEPT_EDGE",EDGE,{"disambiguationData":[OSD([subQ0,subQ21,subQ20,subQ19,subQ18,subQ17,subQ16,subQ15,subQ14,subQ13,subQ12,subQ11,subQ10,subQ9,subQ8,subQ7,subQ6,subQ5,subQ4,subQ3,subQ2,subQ1]),TDD([makeQuery(id+"F5.imprint","INTERSECT",VERTEX,{"derivedFrom":[makeQuery(id+"F4.boolean.opBoolean","COPY",EDGE,{"derivedFrom":makeQuery(id+"F4.opExtrude","TWEAK_EDGE",EDGE,{"derivedFrom":[subQ22,makeQuery(id+"F2.opShell","OFFSET_EDGE",EDGE,{"disambiguationData":[OSD([subQ12]),TDD([makeQuery(id+"F1.opExtrude","CAP_EDGE",EDGE,{"disambiguationData":[OSD([subQ12])],"isStart":true})])]})]})}),makeQuery(id+"F4.boolean.opBoolean","COPY",EDGE,{"derivedFrom":makeQuery(id+"F4.opExtrude","TWEAK_EDGE",EDGE,{"derivedFrom":[subQ22,makeQuery(id+"F2.opShell","OFFSET_EDGE",EDGE,{"disambiguationData":[OSD([subQ0]),TDD([makeQuery(id+"F1.opExtrude","CAP_EDGE",EDGE,{"disambiguationData":[OSD([subQ0])],"isStart":true})]),OD(0.0)]})]})})]})])]})]});}
            var Q1;
            {var subQ0=sQuery(id+"F0.wireOp",EDGE,"E0");var subQ1=sQuery(id+"F0.wireOp",EDGE,"E21");var subQ2=sQuery(id+"F0.wireOp",EDGE,"E20");var subQ3=sQuery(id+"F0.wireOp",EDGE,"E19");var subQ4=sQuery(id+"F0.wireOp",EDGE,"E18.right");var subQ5=sQuery(id+"F0.wireOp",EDGE,"E18.left");var subQ6=sQuery(id+"F0.wireOp",EDGE,"E17.right");var subQ7=sQuery(id+"F0.wireOp",EDGE,"E17.left");var subQ8=sQuery(id+"F0.wireOp",EDGE,"E16");var subQ9=sQuery(id+"F0.wireOp",EDGE,"E15");var subQ10=sQuery(id+"F0.wireOp",EDGE,"E14");var subQ11=sQuery(id+"F0.wireOp",EDGE,"E13");var subQ12=sQuery(id+"F0.wireOp",EDGE,"E12");var subQ13=sQuery(id+"F0.wireOp",EDGE,"E9.right");var subQ14=sQuery(id+"F0.wireOp",EDGE,"E9.left");var subQ15=sQuery(id+"F0.wireOp",EDGE,"E8.right");var subQ16=sQuery(id+"F0.wireOp",EDGE,"E8.left");var subQ17=sQuery(id+"F0.wireOp",EDGE,"E7");var subQ18=sQuery(id+"F0.wireOp",EDGE,"E6");var subQ19=sQuery(id+"F0.wireOp",EDGE,"E5");var subQ20=sQuery(id+"F0.wireOp",EDGE,"E2.right");var subQ21=sQuery(id+"F0.wireOp",EDGE,"E2.left");var subQ22=makeQuery(id+"F1.opExtrude","CAP_FACE",FACE,{"disambiguationData":[OSD([subQ0,subQ21,subQ20,subQ19,subQ18,subQ17,subQ16,subQ15,subQ14,subQ13,subQ12,subQ11,subQ10,subQ9,subQ8,subQ7,subQ6,subQ5,subQ4,subQ3,subQ2,subQ1])],"isStart":true});var subQ23=makeQuery(id+"F1.opExtrude","SWEPT_FACE",FACE,{"disambiguationData":[OSD([subQ2])]});var subQ24=makeQuery(id+"F1.opExtrude","SWEPT_FACE",FACE,{"disambiguationData":[OSD([subQ0])]});Q1=makeQuery(id+"F6.boolean.opBoolean","MERGE",EDGE,{"derivedFrom":[makeQuery(id+"F4.boolean.opBoolean","MERGE",EDGE,{"derivedFrom":[makeQuery(id+"F2.opShell","TWEAK_EDGE",EDGE,{"derivedFrom":[subQ24,subQ23]}),makeQuery(id+"F4.opExtrude","SWEPT_EDGE",EDGE,{"disambiguationData":[OSD([subQ0,subQ21,subQ20,subQ19,subQ18,subQ17,subQ16,subQ15,subQ14,subQ13,subQ12,subQ11,subQ10,subQ9,subQ8,subQ7,subQ6,subQ5,subQ4,subQ3,subQ2,subQ1]),TDD([makeQuery(id+"F2.opShell","TWEAK_VERTEX",VERTEX,{"derivedFrom":[subQ24,subQ22,subQ23]})])]})]}),makeQuery(id+"F6.opExtrude","SWEPT_EDGE",EDGE,{"disambiguationData":[OSD([subQ0,subQ21,subQ20,subQ19,subQ18,subQ17,subQ16,subQ15,subQ14,subQ13,subQ12,subQ11,subQ10,subQ9,subQ8,subQ7,subQ6,subQ5,subQ4,subQ3,subQ2,subQ1]),TDD([makeQuery(id+"F5.imprint","INTERSECT",VERTEX,{"derivedFrom":[makeQuery(id+"F4.boolean.opBoolean","COPY",EDGE,{"derivedFrom":makeQuery(id+"F4.opExtrude","TWEAK_EDGE",EDGE,{"derivedFrom":[subQ22,makeQuery(id+"F2.opShell","OFFSET_EDGE",EDGE,{"disambiguationData":[OSD([subQ2]),TDD([makeQuery(id+"F1.opExtrude","CAP_EDGE",EDGE,{"disambiguationData":[OSD([subQ2])],"isStart":true})])]})]})}),makeQuery(id+"F4.boolean.opBoolean","COPY",EDGE,{"derivedFrom":makeQuery(id+"F4.opExtrude","TWEAK_EDGE",EDGE,{"derivedFrom":[subQ22,makeQuery(id+"F2.opShell","OFFSET_EDGE",EDGE,{"disambiguationData":[OSD([subQ0]),TDD([makeQuery(id+"F1.opExtrude","CAP_EDGE",EDGE,{"disambiguationData":[OSD([subQ0])],"isStart":true})]),OD(0.0)]})]})})]})])]})]});}
            var Q2;
            {var subQ0=sQuery(id+"F0.wireOp",EDGE,"E5");var subQ1=sQuery(id+"F0.wireOp",EDGE,"E21");var subQ2=sQuery(id+"F0.wireOp",EDGE,"E20");var subQ3=sQuery(id+"F0.wireOp",EDGE,"E19");var subQ4=sQuery(id+"F0.wireOp",EDGE,"E18.right");var subQ5=sQuery(id+"F0.wireOp",EDGE,"E18.left");var subQ6=sQuery(id+"F0.wireOp",EDGE,"E17.right");var subQ7=sQuery(id+"F0.wireOp",EDGE,"E17.left");var subQ8=sQuery(id+"F0.wireOp",EDGE,"E16");var subQ9=sQuery(id+"F0.wireOp",EDGE,"E15");var subQ10=sQuery(id+"F0.wireOp",EDGE,"E14");var subQ11=sQuery(id+"F0.wireOp",EDGE,"E13");var subQ12=sQuery(id+"F0.wireOp",EDGE,"E12");var subQ13=sQuery(id+"F0.wireOp",EDGE,"E9.right");var subQ14=sQuery(id+"F0.wireOp",EDGE,"E9.left");var subQ15=sQuery(id+"F0.wireOp",EDGE,"E8.right");var subQ16=sQuery(id+"F0.wireOp",EDGE,"E8.left");var subQ17=sQuery(id+"F0.wireOp",EDGE,"E7");var subQ18=sQuery(id+"F0.wireOp",EDGE,"E6");var subQ19=sQuery(id+"F0.wireOp",EDGE,"E2.right");var subQ20=sQuery(id+"F0.wireOp",EDGE,"E2.left");var subQ21=sQuery(id+"F0.wireOp",EDGE,"E0");var subQ22=makeQuery(id+"F1.opExtrude","CAP_FACE",FACE,{"disambiguationData":[OSD([subQ21,subQ20,subQ19,subQ0,subQ18,subQ17,subQ16,subQ15,subQ14,subQ13,subQ12,subQ11,subQ10,subQ9,subQ8,subQ7,subQ6,subQ5,subQ4,subQ3,subQ2,subQ1])],"isStart":true});var subQ23=makeQuery(id+"F1.opExtrude","SWEPT_FACE",FACE,{"disambiguationData":[OSD([subQ11])]});var subQ24=makeQuery(id+"F1.opExtrude","SWEPT_FACE",FACE,{"disambiguationData":[OSD([subQ0])]});Q2=makeQuery(id+"F6.boolean.opBoolean","MERGE",EDGE,{"derivedFrom":[makeQuery(id+"F4.boolean.opBoolean","MERGE",EDGE,{"derivedFrom":[makeQuery(id+"F2.opShell","TWEAK_EDGE",EDGE,{"derivedFrom":[subQ24,subQ23]}),makeQuery(id+"F4.opExtrude","SWEPT_EDGE",EDGE,{"disambiguationData":[OSD([subQ21,subQ20,subQ19,subQ0,subQ18,subQ17,subQ16,subQ15,subQ14,subQ13,subQ12,subQ11,subQ10,subQ9,subQ8,subQ7,subQ6,subQ5,subQ4,subQ3,subQ2,subQ1]),TDD([makeQuery(id+"F2.opShell","TWEAK_VERTEX",VERTEX,{"derivedFrom":[subQ22,subQ24,subQ23]})])]})]}),makeQuery(id+"F6.opExtrude","SWEPT_EDGE",EDGE,{"disambiguationData":[OSD([subQ21,subQ20,subQ19,subQ0,subQ18,subQ17,subQ16,subQ15,subQ14,subQ13,subQ12,subQ11,subQ10,subQ9,subQ8,subQ7,subQ6,subQ5,subQ4,subQ3,subQ2,subQ1]),TDD([makeQuery(id+"F5.imprint","INTERSECT",VERTEX,{"derivedFrom":[makeQuery(id+"F4.boolean.opBoolean","COPY",EDGE,{"derivedFrom":makeQuery(id+"F4.opExtrude","TWEAK_EDGE",EDGE,{"derivedFrom":[subQ22,makeQuery(id+"F2.opShell","OFFSET_EDGE",EDGE,{"disambiguationData":[OSD([subQ11]),TDD([makeQuery(id+"F1.opExtrude","CAP_EDGE",EDGE,{"disambiguationData":[OSD([subQ11])],"isStart":true})])]})]})}),makeQuery(id+"F4.boolean.opBoolean","COPY",EDGE,{"derivedFrom":makeQuery(id+"F4.opExtrude","TWEAK_EDGE",EDGE,{"derivedFrom":[subQ22,makeQuery(id+"F2.opShell","OFFSET_EDGE",EDGE,{"disambiguationData":[OSD([subQ0]),TDD([makeQuery(id+"F1.opExtrude","CAP_EDGE",EDGE,{"disambiguationData":[OSD([subQ0])],"isStart":true})]),OD(0.0)]})]})})]})])]})]});}
            var Q3;
            {var subQ0=sQuery(id+"F0.wireOp",EDGE,"E5");var subQ1=sQuery(id+"F0.wireOp",EDGE,"E21");var subQ2=sQuery(id+"F0.wireOp",EDGE,"E20");var subQ3=sQuery(id+"F0.wireOp",EDGE,"E19");var subQ4=sQuery(id+"F0.wireOp",EDGE,"E18.right");var subQ5=sQuery(id+"F0.wireOp",EDGE,"E18.left");var subQ6=sQuery(id+"F0.wireOp",EDGE,"E17.right");var subQ7=sQuery(id+"F0.wireOp",EDGE,"E17.left");var subQ8=sQuery(id+"F0.wireOp",EDGE,"E16");var subQ9=sQuery(id+"F0.wireOp",EDGE,"E15");var subQ10=sQuery(id+"F0.wireOp",EDGE,"E14");var subQ11=sQuery(id+"F0.wireOp",EDGE,"E13");var subQ12=sQuery(id+"F0.wireOp",EDGE,"E12");var subQ13=sQuery(id+"F0.wireOp",EDGE,"E9.right");var subQ14=sQuery(id+"F0.wireOp",EDGE,"E9.left");var subQ15=sQuery(id+"F0.wireOp",EDGE,"E8.right");var subQ16=sQuery(id+"F0.wireOp",EDGE,"E8.left");var subQ17=sQuery(id+"F0.wireOp",EDGE,"E7");var subQ18=sQuery(id+"F0.wireOp",EDGE,"E6");var subQ19=sQuery(id+"F0.wireOp",EDGE,"E2.right");var subQ20=sQuery(id+"F0.wireOp",EDGE,"E2.left");var subQ21=sQuery(id+"F0.wireOp",EDGE,"E0");var subQ22=makeQuery(id+"F1.opExtrude","CAP_FACE",FACE,{"disambiguationData":[OSD([subQ21,subQ20,subQ19,subQ0,subQ18,subQ17,subQ16,subQ15,subQ14,subQ13,subQ12,subQ11,subQ10,subQ9,subQ8,subQ7,subQ6,subQ5,subQ4,subQ3,subQ2,subQ1])],"isStart":true});var subQ23=makeQuery(id+"F1.opExtrude","SWEPT_FACE",FACE,{"disambiguationData":[OSD([subQ1])]});var subQ24=makeQuery(id+"F1.opExtrude","SWEPT_FACE",FACE,{"disambiguationData":[OSD([subQ0])]});Q3=makeQuery(id+"F6.boolean.opBoolean","MERGE",EDGE,{"derivedFrom":[makeQuery(id+"F4.boolean.opBoolean","MERGE",EDGE,{"derivedFrom":[makeQuery(id+"F2.opShell","TWEAK_EDGE",EDGE,{"derivedFrom":[subQ24,subQ23]}),makeQuery(id+"F4.opExtrude","SWEPT_EDGE",EDGE,{"disambiguationData":[OSD([subQ21,subQ20,subQ19,subQ0,subQ18,subQ17,subQ16,subQ15,subQ14,subQ13,subQ12,subQ11,subQ10,subQ9,subQ8,subQ7,subQ6,subQ5,subQ4,subQ3,subQ2,subQ1]),TDD([makeQuery(id+"F2.opShell","TWEAK_VERTEX",VERTEX,{"derivedFrom":[subQ22,subQ24,subQ23]})])]})]}),makeQuery(id+"F6.opExtrude","SWEPT_EDGE",EDGE,{"disambiguationData":[OSD([subQ21,subQ20,subQ19,subQ0,subQ18,subQ17,subQ16,subQ15,subQ14,subQ13,subQ12,subQ11,subQ10,subQ9,subQ8,subQ7,subQ6,subQ5,subQ4,subQ3,subQ2,subQ1]),TDD([makeQuery(id+"F5.imprint","INTERSECT",VERTEX,{"derivedFrom":[makeQuery(id+"F4.boolean.opBoolean","COPY",EDGE,{"derivedFrom":makeQuery(id+"F4.opExtrude","TWEAK_EDGE",EDGE,{"derivedFrom":[subQ22,makeQuery(id+"F2.opShell","OFFSET_EDGE",EDGE,{"disambiguationData":[OSD([subQ1]),TDD([makeQuery(id+"F1.opExtrude","CAP_EDGE",EDGE,{"disambiguationData":[OSD([subQ1])],"isStart":true})])]})]})}),makeQuery(id+"F4.boolean.opBoolean","COPY",EDGE,{"derivedFrom":makeQuery(id+"F4.opExtrude","TWEAK_EDGE",EDGE,{"derivedFrom":[subQ22,makeQuery(id+"F2.opShell","OFFSET_EDGE",EDGE,{"disambiguationData":[OSD([subQ0]),TDD([makeQuery(id+"F1.opExtrude","CAP_EDGE",EDGE,{"disambiguationData":[OSD([subQ0])],"isStart":true})]),OD(0.0)]})]})})]})])]})]});}
            fillet(context, id + "F9", {"entities" : qUnion([Q0, Q1, Q2, Q3]), "radius" : 0.76 * mm, "tangentPropagation" : true, "allowEdgeOverflow" : false});
        }
    });
